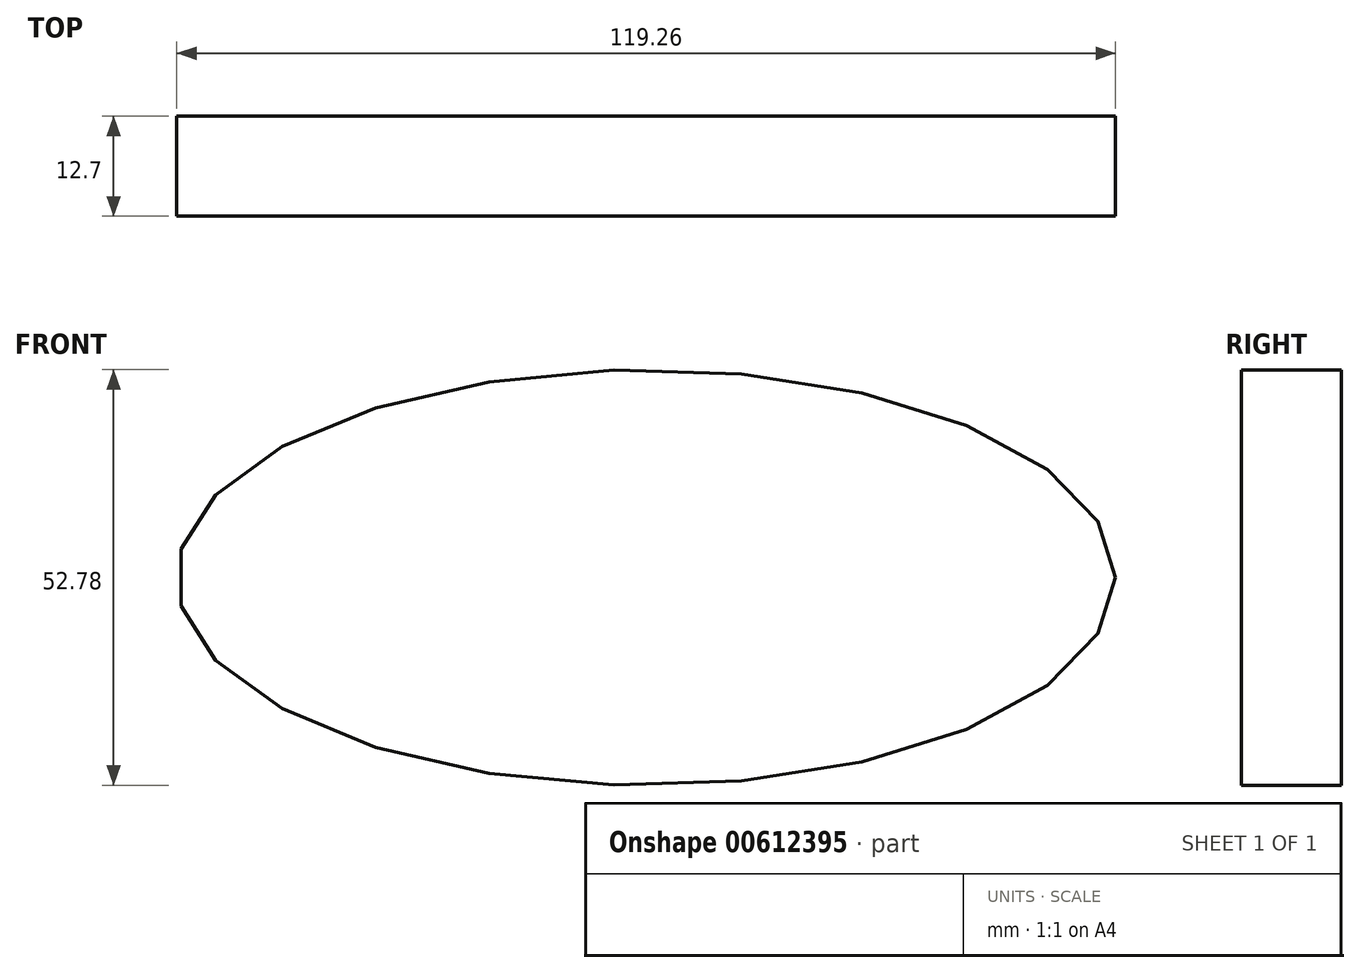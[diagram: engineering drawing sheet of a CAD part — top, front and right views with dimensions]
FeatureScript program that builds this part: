
annotation { "Feature Type Name" : "Feature", "Feature Type Description" : "" }
export const myFeature = defineFeature(function(context is Context, id is Id, definition is map)
    precondition{}
    {
        {
            var Q0;
            Q0=qCreatedBy(makeId("Front.planeOp"),FACE);
            var sketch = newSketch(context, id + "F0", { "sketchPlane" : qUnion([Q0])});
            skEllipse(sketch, "E0", {"center": v(0, -11.91) * mm, "majorRadius": 59.63 * mm, "minorRadius": 26.39 * mm, "majorAxis": v(1, 0)});
            skSolve(sketch);
        }
        {
            var Q0;
            Q0 = qSketchRegion(id + "F0", true);
            extrude(context, id + "F1", {"entities" : qUnion([Q0]), "depth" : 6.35 * mm, "offsetDistance" : 25.4 * mm});
        }
        {
            var Q0;
            Q0=makeQuery(id+"F1.opExtrude","CAP_FACE",FACE,{"disambiguationData":[OSD([sQuery(id+"F0.wireOp",EDGE,"E0")])],"isStart":false});
            var Q1;
            Q1 = qSketchRegion(id + "F0", true);
            extrude(context, id + "F2", {"entities" : qUnion([Q0, Q1]), "operationType" : NewBodyOperationType.ADD, "oppositeDirection" : true, "depth" : 6.35 * mm, "offsetDistance" : 25.4 * mm});
        }
    });
